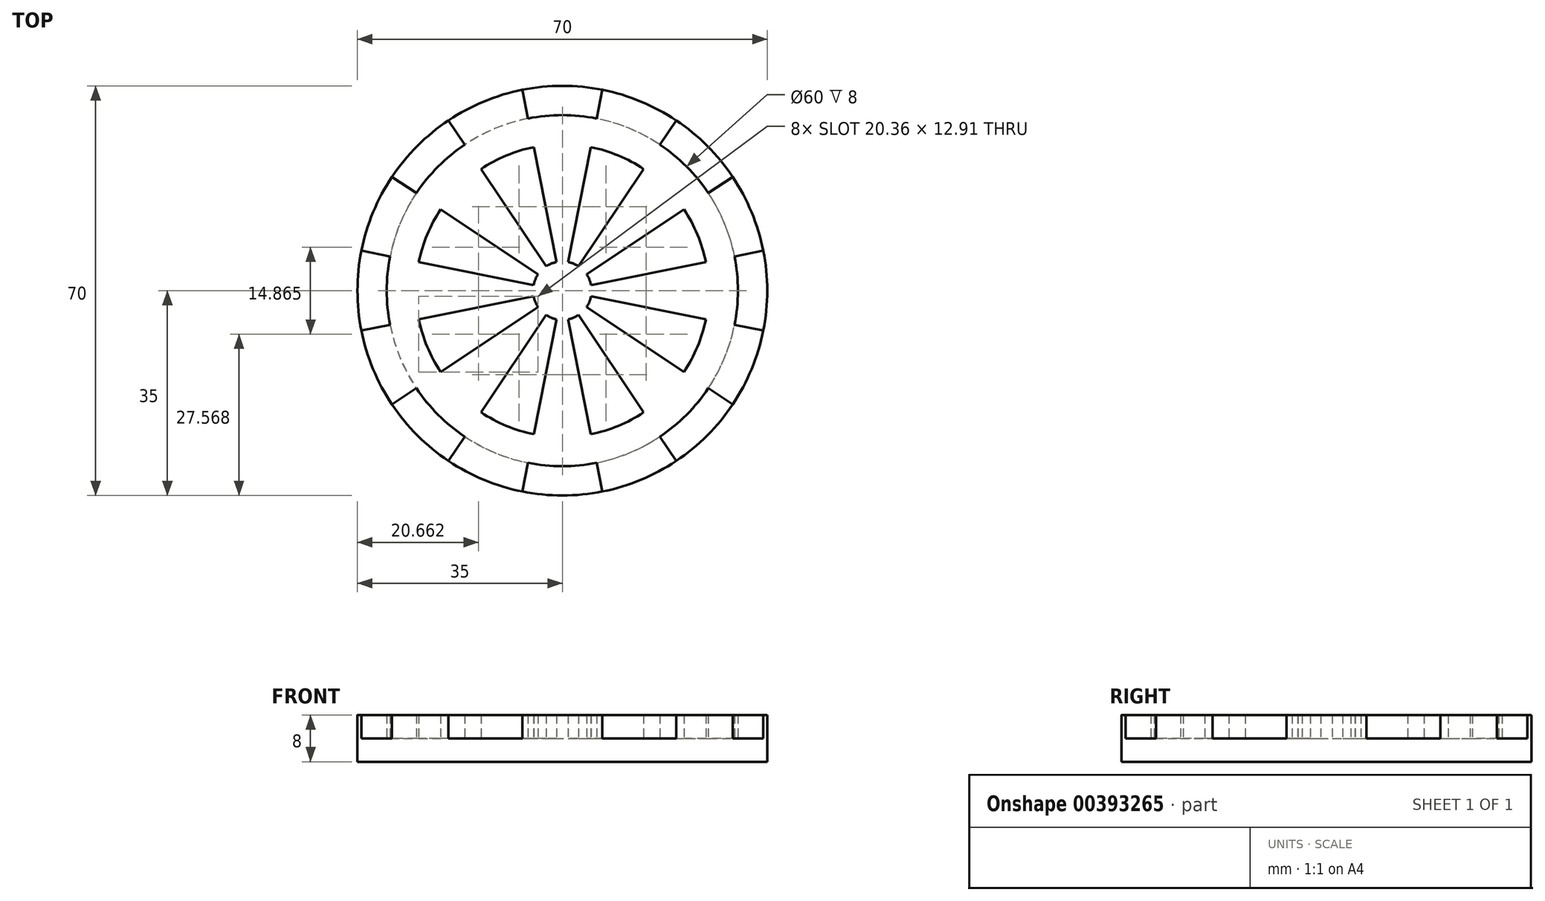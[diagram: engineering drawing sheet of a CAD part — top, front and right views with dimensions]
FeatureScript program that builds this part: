
annotation { "Feature Type Name" : "Feature", "Feature Type Description" : "" }
export const myFeature = defineFeature(function(context is Context, id is Id, definition is map)
    precondition{}
    {
        {
            var Q0;
            Q0=qCreatedBy(makeId("Top.planeOp"),FACE);
            var sketch = newSketch(context, id + "F0", { "sketchPlane" : qUnion([Q0])});
            skCircle(sketch, "E0", {"center": v(0, 0) * mm, "radius": 30 * mm});
            skCircle(sketch, "E1", {"center": v(0, 0) * mm, "radius": 35 * mm});
            skSolve(sketch);
        }
        {
            var Q0;
            Q0 = qSketchRegion(id + "F0", true);
            extrude(context, id + "F1", {"entities" : qUnion([Q0]), "depth" : 4 * mm});
        }
        {
            var Q0;
            Q0=makeQuery(id+"F1.opExtrude","CAP_FACE",FACE,{"disambiguationData":[OSD([sQuery(id+"F0.wireOp",EDGE,"E0"),sQuery(id+"F0.wireOp",EDGE,"E1")])],"isStart":false});
            var sketch = newSketch(context, id + "F2", { "sketchPlane" : qUnion([Q0])});
            skPoint(sketch, "E2.0", {"position": v(0, 0) * mm});
            skLineSegment(sketch, "E3", {"start": v(-5.85, 29.42) * mm, "end": v(-6.83, 34.33) * mm});
            skLineSegment(sketch, "E4", {"start": v(5.85, 29.42) * mm, "end": v(6.83, 34.33) * mm});
            skArc(sketch, "E5.0.0", {"start": v(6.83, 34.33) * mm, "mid": v(0, 35) * mm, "end": v(-6.83, 34.33) * mm});
            skArc(sketch, "E6.0", {"start": v(5.85, 29.42) * mm, "mid": v(0, 30) * mm, "end": v(-5.85, 29.42) * mm});
            skLineSegment(sketch, "E7.1.0", {"start": v(-16.67, 24.94) * mm, "end": v(-19.44, 29.1) * mm});
            skLineSegment(sketch, "E7.1.1", {"start": v(-24.94, 16.67) * mm, "end": v(-29.1, 19.44) * mm});
            skArc(sketch, "E7.1.2", {"start": v(-19.44, 29.1) * mm, "mid": v(-24.75, 24.75) * mm, "end": v(-29.1, 19.44) * mm});
            skArc(sketch, "E7.1.3", {"start": v(-16.67, 24.94) * mm, "mid": v(-21.21, 21.21) * mm, "end": v(-24.94, 16.67) * mm});
            skLineSegment(sketch, "E7.2.0", {"start": v(-29.42, 5.85) * mm, "end": v(-34.33, 6.83) * mm});
            skLineSegment(sketch, "E7.2.1", {"start": v(-29.42, -5.85) * mm, "end": v(-34.33, -6.83) * mm});
            skArc(sketch, "E7.2.2", {"start": v(-34.33, 6.83) * mm, "mid": v(-35, 0) * mm, "end": v(-34.33, -6.83) * mm});
            skArc(sketch, "E7.2.3", {"start": v(-29.42, 5.85) * mm, "mid": v(-30, 0) * mm, "end": v(-29.42, -5.85) * mm});
            skLineSegment(sketch, "E7.3.0", {"start": v(-24.94, -16.67) * mm, "end": v(-29.1, -19.44) * mm});
            skLineSegment(sketch, "E7.3.1", {"start": v(-16.67, -24.94) * mm, "end": v(-19.44, -29.1) * mm});
            skArc(sketch, "E7.3.2", {"start": v(-29.1, -19.44) * mm, "mid": v(-24.75, -24.75) * mm, "end": v(-19.44, -29.1) * mm});
            skArc(sketch, "E7.3.3", {"start": v(-24.94, -16.67) * mm, "mid": v(-21.21, -21.21) * mm, "end": v(-16.67, -24.94) * mm});
            skLineSegment(sketch, "E7.4.0", {"start": v(-5.85, -29.42) * mm, "end": v(-6.83, -34.33) * mm});
            skLineSegment(sketch, "E7.4.1", {"start": v(5.85, -29.42) * mm, "end": v(6.83, -34.33) * mm});
            skArc(sketch, "E7.4.2", {"start": v(-6.83, -34.33) * mm, "mid": v(0, -35) * mm, "end": v(6.83, -34.33) * mm});
            skArc(sketch, "E7.4.3", {"start": v(-5.85, -29.42) * mm, "mid": v(0, -30) * mm, "end": v(5.85, -29.42) * mm});
            skLineSegment(sketch, "E7.5.0", {"start": v(16.67, -24.94) * mm, "end": v(19.44, -29.1) * mm});
            skLineSegment(sketch, "E7.5.1", {"start": v(24.94, -16.67) * mm, "end": v(29.1, -19.44) * mm});
            skArc(sketch, "E7.5.2", {"start": v(19.44, -29.1) * mm, "mid": v(24.75, -24.75) * mm, "end": v(29.1, -19.44) * mm});
            skArc(sketch, "E7.5.3", {"start": v(16.67, -24.94) * mm, "mid": v(21.21, -21.21) * mm, "end": v(24.94, -16.67) * mm});
            skLineSegment(sketch, "E7.6.0", {"start": v(29.42, -5.85) * mm, "end": v(34.33, -6.83) * mm});
            skLineSegment(sketch, "E7.6.1", {"start": v(29.42, 5.85) * mm, "end": v(34.33, 6.83) * mm});
            skArc(sketch, "E7.6.2", {"start": v(34.33, -6.83) * mm, "mid": v(35, 0) * mm, "end": v(34.33, 6.83) * mm});
            skArc(sketch, "E7.6.3", {"start": v(29.42, -5.85) * mm, "mid": v(30, 0) * mm, "end": v(29.42, 5.85) * mm});
            skLineSegment(sketch, "E7.7.0", {"start": v(24.94, 16.67) * mm, "end": v(29.1, 19.44) * mm});
            skLineSegment(sketch, "E7.7.1", {"start": v(16.67, 24.94) * mm, "end": v(19.44, 29.1) * mm});
            skArc(sketch, "E7.7.2", {"start": v(29.1, 19.44) * mm, "mid": v(24.75, 24.75) * mm, "end": v(19.44, 29.1) * mm});
            skArc(sketch, "E7.7.3", {"start": v(24.94, 16.67) * mm, "mid": v(21.21, 21.21) * mm, "end": v(16.67, 24.94) * mm});
            skSolve(sketch);
        }
        {
            var Q0;
            Q0 = qSketchRegion(id + "F2", true);
            extrude(context, id + "F3", {"entities" : qUnion([Q0]), "operationType" : NewBodyOperationType.ADD, "depth" : 4 * mm});
        }
        {
            var Q0;
            {var subQ0=sQuery(id+"F0.wireOp",EDGE,"E1");var subQ1=sQuery(id+"F0.wireOp",EDGE,"E0");Q0=makeQuery(id+"F3.boolean.opBoolean","SPLIT",FACE,{"disambiguationData":[TD([makeQuery(id+"F3.opExtrude","SWEPT_FACE",FACE,{"disambiguationData":[OSD([sQuery(id+"F2.wireOp",EDGE,"E7.3.1")])]})])],"derivedFrom":makeQuery(id+"F1.opExtrude","CAP_FACE",FACE,{"disambiguationData":[OSD([subQ1,subQ0])],"isStart":false})});}
            var sketch = newSketch(context, id + "F4", { "sketchPlane" : qUnion([Q0])});
            skArc(sketch, "E8.0", {"start": v(-29.1, 19.44) * mm, "mid": v(-32.34, 13.4) * mm, "end": v(-34.33, 6.83) * mm});
            skLineSegment(sketch, "E9.0", {"start": v(-24.94, 16.67) * mm, "end": v(-29.1, 19.44) * mm});
            skLineSegment(sketch, "E10.0", {"start": v(-29.42, 5.85) * mm, "end": v(-34.33, 6.83) * mm});
            skArc(sketch, "E11.0", {"start": v(-29.42, 5.85) * mm, "mid": v(-30, 0) * mm, "end": v(-29.42, -5.85) * mm});
            skLineSegment(sketch, "E12.1.0", {"start": v(-29.42, -5.85) * mm, "end": v(-34.33, -6.83) * mm});
            skArc(sketch, "E12.1.1", {"start": v(-34.33, -6.83) * mm, "mid": v(-32.34, -13.4) * mm, "end": v(-29.1, -19.44) * mm});
            skLineSegment(sketch, "E12.1.2", {"start": v(-24.94, -16.67) * mm, "end": v(-29.1, -19.44) * mm});
            skArc(sketch, "E12.1.3", {"start": v(-24.94, -16.67) * mm, "mid": v(-21.21, -21.21) * mm, "end": v(-16.67, -24.94) * mm});
            skLineSegment(sketch, "E12.2.0", {"start": v(-16.67, -24.94) * mm, "end": v(-19.44, -29.1) * mm});
            skArc(sketch, "E12.2.1", {"start": v(-19.44, -29.1) * mm, "mid": v(-13.4, -32.34) * mm, "end": v(-6.83, -34.33) * mm});
            skLineSegment(sketch, "E12.2.2", {"start": v(-5.85, -29.42) * mm, "end": v(-6.83, -34.33) * mm});
            skArc(sketch, "E12.2.3", {"start": v(-5.85, -29.42) * mm, "mid": v(0, -30) * mm, "end": v(5.85, -29.42) * mm});
            skLineSegment(sketch, "E12.3.0", {"start": v(5.85, -29.42) * mm, "end": v(6.83, -34.33) * mm});
            skArc(sketch, "E12.3.1", {"start": v(6.83, -34.33) * mm, "mid": v(13.4, -32.34) * mm, "end": v(19.44, -29.1) * mm});
            skLineSegment(sketch, "E12.3.2", {"start": v(16.67, -24.94) * mm, "end": v(19.44, -29.1) * mm});
            skArc(sketch, "E12.3.3", {"start": v(16.67, -24.94) * mm, "mid": v(21.21, -21.21) * mm, "end": v(24.94, -16.67) * mm});
            skLineSegment(sketch, "E12.4.0", {"start": v(24.94, -16.67) * mm, "end": v(29.1, -19.44) * mm});
            skArc(sketch, "E12.4.1", {"start": v(29.1, -19.44) * mm, "mid": v(32.34, -13.4) * mm, "end": v(34.33, -6.83) * mm});
            skLineSegment(sketch, "E12.4.2", {"start": v(29.42, -5.85) * mm, "end": v(34.33, -6.83) * mm});
            skArc(sketch, "E12.4.3", {"start": v(29.42, -5.85) * mm, "mid": v(30, 0) * mm, "end": v(29.42, 5.85) * mm});
            skLineSegment(sketch, "E12.5.0", {"start": v(29.42, 5.85) * mm, "end": v(34.33, 6.83) * mm});
            skArc(sketch, "E12.5.1", {"start": v(34.33, 6.83) * mm, "mid": v(32.34, 13.4) * mm, "end": v(29.1, 19.44) * mm});
            skLineSegment(sketch, "E12.5.2", {"start": v(24.94, 16.67) * mm, "end": v(29.1, 19.44) * mm});
            skArc(sketch, "E12.5.3", {"start": v(24.94, 16.67) * mm, "mid": v(21.21, 21.21) * mm, "end": v(16.67, 24.94) * mm});
            skLineSegment(sketch, "E12.6.0", {"start": v(16.67, 24.94) * mm, "end": v(19.44, 29.1) * mm});
            skArc(sketch, "E12.6.1", {"start": v(19.44, 29.1) * mm, "mid": v(13.4, 32.34) * mm, "end": v(6.83, 34.33) * mm});
            skLineSegment(sketch, "E12.6.2", {"start": v(5.85, 29.42) * mm, "end": v(6.83, 34.33) * mm});
            skArc(sketch, "E12.6.3", {"start": v(5.85, 29.42) * mm, "mid": v(0, 30) * mm, "end": v(-5.85, 29.42) * mm});
            skLineSegment(sketch, "E12.7.0", {"start": v(-5.85, 29.42) * mm, "end": v(-6.83, 34.33) * mm});
            skArc(sketch, "E12.7.1", {"start": v(-6.83, 34.33) * mm, "mid": v(-13.4, 32.34) * mm, "end": v(-19.44, 29.1) * mm});
            skLineSegment(sketch, "E12.7.2", {"start": v(-16.67, 24.94) * mm, "end": v(-19.44, 29.1) * mm});
            skArc(sketch, "E12.7.3", {"start": v(-16.67, 24.94) * mm, "mid": v(-21.21, 21.21) * mm, "end": v(-24.94, 16.67) * mm});
            skArc(sketch, "E13", {"start": v(-4.88, 24.52) * mm, "mid": v(-9.57, 23.1) * mm, "end": v(-13.89, 20.79) * mm});
            skLineSegment(sketch, "E14", {"start": v(-0.98, 4.9) * mm, "end": v(-4.88, 24.52) * mm});
            skLineSegment(sketch, "E15.1.0", {"start": v(0.98, 4.9) * mm, "end": v(4.88, 24.52) * mm});
            skLineSegment(sketch, "E15.2.0", {"start": v(2.78, 4.16) * mm, "end": v(13.89, 20.79) * mm});
            skLineSegment(sketch, "E15.3.0", {"start": v(4.16, 2.78) * mm, "end": v(20.79, 13.89) * mm});
            skLineSegment(sketch, "E15.4.0", {"start": v(4.9, 0.98) * mm, "end": v(24.52, 4.88) * mm});
            skLineSegment(sketch, "E15.6.0", {"start": v(4.16, -2.78) * mm, "end": v(20.79, -13.89) * mm});
            skLineSegment(sketch, "E15.7.0", {"start": v(0, 0) * mm, "end": v(13.89, -20.79) * mm});
            skLineSegment(sketch, "E15.8.0", {"start": v(0.98, -4.9) * mm, "end": v(4.88, -24.52) * mm});
            skLineSegment(sketch, "E15.9.0", {"start": v(-0.98, -4.9) * mm, "end": v(-4.88, -24.52) * mm});
            skLineSegment(sketch, "E15.10.0", {"start": v(-2.78, -4.16) * mm, "end": v(-13.89, -20.79) * mm});
            skLineSegment(sketch, "E15.11.0", {"start": v(-4.16, -2.78) * mm, "end": v(-20.79, -13.89) * mm});
            skLineSegment(sketch, "E15.12.0", {"start": v(-4.9, -0.98) * mm, "end": v(-24.52, -4.88) * mm});
            skLineSegment(sketch, "E15.13.0", {"start": v(-4.9, 0.98) * mm, "end": v(-24.52, 4.88) * mm});
            skLineSegment(sketch, "E15.14.0", {"start": v(-4.16, 2.78) * mm, "end": v(-20.79, 13.89) * mm});
            skLineSegment(sketch, "E15.15.0", {"start": v(0, 0) * mm, "end": v(-13.89, 20.79) * mm});
            skLineSegment(sketch, "E15.anchor1", {"start": v(-0.98, 4.9) * mm, "end": v(-4.88, 24.52) * mm, "construction": true});
            skLineSegment(sketch, "E15.anchor2", {"start": v(0, 0) * mm, "end": v(-13.89, 20.79) * mm, "construction": true});
            skArc(sketch, "E16.trimOffspring", {"start": v(13.89, 20.79) * mm, "mid": v(9.57, 23.1) * mm, "end": v(4.88, 24.52) * mm});
            skArc(sketch, "E17.trimOffspring", {"start": v(24.52, 4.88) * mm, "mid": v(23.1, 9.57) * mm, "end": v(20.79, 13.89) * mm});
            skArc(sketch, "E18.trimOffspring", {"start": v(20.79, -13.89) * mm, "mid": v(23.1, -9.57) * mm, "end": v(24.52, -4.88) * mm});
            skArc(sketch, "E19.trimOffspring", {"start": v(4.88, -24.52) * mm, "mid": v(9.57, -23.1) * mm, "end": v(13.89, -20.79) * mm});
            skArc(sketch, "E20.trimOffspring", {"start": v(-13.89, -20.79) * mm, "mid": v(-9.57, -23.1) * mm, "end": v(-4.88, -24.52) * mm});
            skArc(sketch, "E21.trimOffspring", {"start": v(-24.52, -4.88) * mm, "mid": v(-23.1, -9.57) * mm, "end": v(-20.79, -13.89) * mm});
            skArc(sketch, "E22.trimOffspring", {"start": v(-20.79, 13.89) * mm, "mid": v(-23.1, 9.57) * mm, "end": v(-24.52, 4.88) * mm});
            skArc(sketch, "E23", {"start": v(4.9, 0.98) * mm, "mid": v(4.62, 1.91) * mm, "end": v(4.16, 2.78) * mm});
            skLineSegment(sketch, "E24", {"start": v(24.52, -4.88) * mm, "end": v(4.9, -0.98) * mm});
            skArc(sketch, "E25.trimOffspring", {"start": v(4.16, -2.78) * mm, "mid": v(4.62, -1.91) * mm, "end": v(4.9, -0.98) * mm});
            skArc(sketch, "E26.trimOffspring", {"start": v(0.98, -4.9) * mm, "mid": v(1.91, -4.62) * mm, "end": v(2.78, -4.16) * mm});
            skArc(sketch, "E27.trimOffspring", {"start": v(-2.78, -4.16) * mm, "mid": v(-1.91, -4.62) * mm, "end": v(-0.98, -4.9) * mm});
            skArc(sketch, "E28.trimOffspring", {"start": v(-4.9, -0.98) * mm, "mid": v(-4.62, -1.91) * mm, "end": v(-4.16, -2.78) * mm});
            skArc(sketch, "E29.trimOffspring", {"start": v(-4.16, 2.78) * mm, "mid": v(-4.62, 1.91) * mm, "end": v(-4.9, 0.98) * mm});
            skArc(sketch, "E30.trimOffspring", {"start": v(-0.98, 4.9) * mm, "mid": v(-1.91, 4.62) * mm, "end": v(-2.78, 4.16) * mm});
            skArc(sketch, "E31.trimOffspring", {"start": v(2.78, 4.16) * mm, "mid": v(1.91, 4.62) * mm, "end": v(0.98, 4.9) * mm});
            skSolve(sketch);
        }
        {
            var Q0;
            Q0 = qSketchRegion(id + "F4", true);
            extrude(context, id + "F5", {"entities" : qUnion([Q0]), "depth" : 4 * mm});
        }
    });
